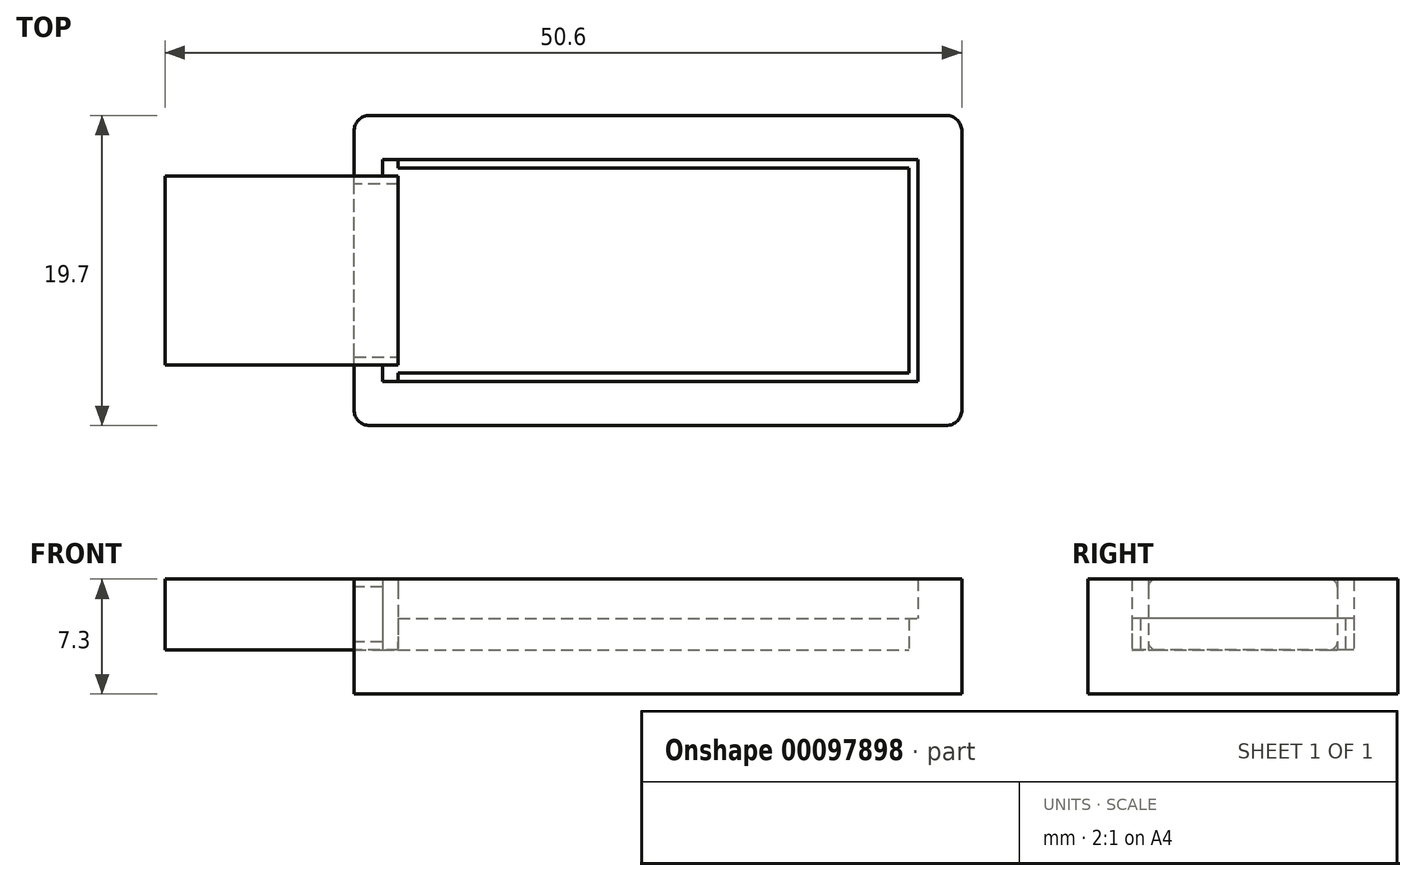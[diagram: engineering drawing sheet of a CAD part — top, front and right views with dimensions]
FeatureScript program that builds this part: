
annotation { "Feature Type Name" : "Feature", "Feature Type Description" : "" }
export const myFeature = defineFeature(function(context is Context, id is Id, definition is map)
    precondition{}
    {
        {
            var Q0;
            Q0=qCreatedBy(makeId("Top.planeOp"),FACE);
            var sketch = newSketch(context, id + "F0", { "sketchPlane" : qUnion([Q0])});
            skLineSegment(sketch, "E0.bottom", {"start": v(-43.45, 19.68) * mm, "end": v(-9.45, 19.68) * mm});
            skLineSegment(sketch, "E0.top", {"start": v(-43.45, 5.58) * mm, "end": v(-9.45, 5.58) * mm});
            skLineSegment(sketch, "E0.left", {"start": v(-42.45, 19.68) * mm, "end": v(-42.45, 18.63) * mm});
            skLineSegment(sketch, "E0.right", {"start": v(-9.45, 19.68) * mm, "end": v(-9.45, 5.58) * mm});
            skPoint(sketch, "E1", {"position": v(-42.45, 12.63) * mm});
            skLineSegment(sketch, "E2.bottom", {"start": v(-42.45, 12.63) * mm, "end": v(-57.25, 12.63) * mm});
            skLineSegment(sketch, "E2.top", {"start": v(-42.45, 18.63) * mm, "end": v(-57.25, 18.63) * mm});
            skLineSegment(sketch, "E2.left", {"start": v(-42.45, 12.63) * mm, "end": v(-42.45, 18.63) * mm});
            skLineSegment(sketch, "E2.right", {"start": v(-57.25, 12.63) * mm, "end": v(-57.25, 18.63) * mm});
            skLineSegment(sketch, "E3", {"start": v(-57.25, 12.63) * mm, "end": v(-57.25, 6.63) * mm});
            skLineSegment(sketch, "E4", {"start": v(-57.25, 6.63) * mm, "end": v(-42.45, 6.63) * mm});
            skLineSegment(sketch, "E5", {"start": v(-42.45, 18.63) * mm, "end": v(-42.45, 18.63) * mm});
            skLineSegment(sketch, "E6", {"start": v(-42.45, 18.63) * mm, "end": v(-42.45, 6.63) * mm});
            skLineSegment(sketch, "E7", {"start": v(-42.45, 6.63) * mm, "end": v(-42.45, 5.58) * mm});
            skLineSegment(sketch, "E8.0", {"start": v(-45.25, 22.48) * mm, "end": v(-45.25, 18.63) * mm});
            skLineSegment(sketch, "E8.1", {"start": v(-45.25, 6.63) * mm, "end": v(-45.25, 2.78) * mm});
            skLineSegment(sketch, "E8.2", {"start": v(-45.25, 2.78) * mm, "end": v(-6.65, 2.78) * mm});
            skLineSegment(sketch, "E8.3", {"start": v(-6.65, 22.48) * mm, "end": v(-6.65, 2.78) * mm});
            skLineSegment(sketch, "E8.4", {"start": v(-45.25, 22.48) * mm, "end": v(-6.65, 22.48) * mm});
            skLineSegment(sketch, "E9.0", {"start": v(-42.45, 6.13) * mm, "end": v(-10, 6.13) * mm});
            skLineSegment(sketch, "E9.1", {"start": v(-10, 19.13) * mm, "end": v(-10, 6.13) * mm});
            skLineSegment(sketch, "E9.2", {"start": v(-42.45, 19.13) * mm, "end": v(-10, 19.13) * mm});
            skLineSegment(sketch, "E10", {"start": v(-43.45, 19.68) * mm, "end": v(-43.45, 18.63) * mm});
            skLineSegment(sketch, "E11", {"start": v(-43.45, 5.58) * mm, "end": v(-43.45, 6.63) * mm});
            skSolve(sketch);
        }
        {
            var Q0;
            {var subQ5=sQuery(id+"F0.wireOp",EDGE,"E2.bottom");Q0=makeQuery(id+"F0.imprint","IMPRINT",FACE,{"disambiguationData":[TD([[makeQuery(id+"F0.imprint","IMPRINT",EDGE,{"derivedFrom":subQ5}),-1.0]])]});}
            var Q1;
            {var subQ5=sQuery(id+"F0.wireOp",EDGE,"E2.bottom");Q1=makeQuery(id+"F0.imprint","IMPRINT",FACE,{"disambiguationData":[TD([[makeQuery(id+"F0.imprint","IMPRINT",EDGE,{"derivedFrom":subQ5}),1.0]])]});}
            extrude(context, id + "F1", {"entities" : qUnion([Q0, Q1]), "depth" : 4.5 * mm});
        }
        {
            var Q0;
            Q0=makeQuery(id+"F1.opExtrude","CAP_EDGE",EDGE,{"disambiguationData":[OSD([sQuery(id+"F0.wireOp",EDGE,"E4")])],"isStart":false});
            var Q1;
            Q1=makeQuery(id+"F1.opExtrude","CAP_EDGE",EDGE,{"disambiguationData":[OSD([sQuery(id+"F0.wireOp",EDGE,"E4")])],"isStart":true});
            var Q2;
            Q2=makeQuery(id+"F1.opExtrude","CAP_EDGE",EDGE,{"disambiguationData":[OSD([sQuery(id+"F0.wireOp",EDGE,"E2.top")])],"isStart":true});
            var Q3;
            Q3=makeQuery(id+"F1.opExtrude","CAP_EDGE",EDGE,{"disambiguationData":[OSD([sQuery(id+"F0.wireOp",EDGE,"E2.top")])],"isStart":false});
            fillet(context, id + "F2", {"entities" : qUnion([Q0, Q1, Q2, Q3]), "radius" : .5 * mm, "tangentPropagation" : true, "allowEdgeOverflow" : false});
        }
        {
            var Q0;
            Q0=qCreatedBy(makeId("Top.planeOp"),FACE);
            var sketch = newSketch(context, id + "F3", { "sketchPlane" : qUnion([Q0])});
            skPoint(sketch, "E12.0", {"position": v(-45.25, 2.78) * mm});
            skPoint(sketch, "E12.1", {"position": v(-6.65, 2.78) * mm});
            skPoint(sketch, "E12.2", {"position": v(-6.65, 22.48) * mm});
            skPoint(sketch, "E12.3", {"position": v(-45.25, 22.48) * mm});
            skLineSegment(sketch, "E13.bottom", {"start": v(-45.25, 2.78) * mm, "end": v(-6.65, 2.78) * mm});
            skLineSegment(sketch, "E13.top", {"start": v(-45.25, 22.48) * mm, "end": v(-6.65, 22.48) * mm});
            skLineSegment(sketch, "E13.left", {"start": v(-45.25, 2.78) * mm, "end": v(-45.25, 22.48) * mm});
            skLineSegment(sketch, "E13.right", {"start": v(-6.65, 2.78) * mm, "end": v(-6.65, 22.48) * mm});
            skSolve(sketch);
        }
        {
            var Q0;
            Q0 = qSketchRegion(id + "F3", true);
            extrude(context, id + "F4", {"entities" : qUnion([Q0]), "oppositeDirection" : true, "depth" : 2.8 * mm});
        }
        {
            var Q0;
            {var subQ11=sQuery(id+"F0.wireOp",EDGE,"E0.bottom");Q0=makeQuery(id+"F0.imprint","IMPRINT",FACE,{"disambiguationData":[TD([[makeQuery(id+"F0.imprint","IMPRINT",EDGE,{"derivedFrom":subQ11}),1.0]])]});}
            extrude(context, id + "F5", {"entities" : qUnion([Q0]), "operationType" : NewBodyOperationType.ADD, "depth" : 4.5 * mm});
        }
        {
            var Q0;
            {var subQ0=sQuery(id+"F0.wireOp",EDGE,"E0.right");Q0=makeQuery(id+"F0.imprint","IMPRINT",FACE,{"disambiguationData":[TD([[makeQuery(id+"F0.imprint","IMPRINT",EDGE,{"derivedFrom":subQ0}),-1.0]])]});}
            extrude(context, id + "F6", {"entities" : qUnion([Q0]), "operationType" : NewBodyOperationType.ADD, "depth" : 2 * mm});
        }
        {
            var Q0;
            Q0=makeQuery(id+"F5.opExtrude","SWEPT_FACE",FACE,{"disambiguationData":[OSD([sQuery(id+"F0.wireOp",EDGE,"E0.right")])]});
            var sketch = newSketch(context, id + "F7", { "sketchPlane" : qUnion([Q0])});
            skLineSegment(sketch, "E14.0", {"start": v(-19.68, 4.5) * mm, "end": v(-5.58, 4.5) * mm});
            skLineSegment(sketch, "E14.1", {"start": v(-19.68, 4.5) * mm, "end": v(-19.68, 2.8) * mm});
            skLineSegment(sketch, "E14.2", {"start": v(-5.58, 4.5) * mm, "end": v(-5.58, 2.8) * mm});
            skPoint(sketch, "E15.end.orphan", {"position": v(-19.68, 2) * mm});
            skPoint(sketch, "E16.end.orphan", {"position": v(-5.58, 2) * mm});
            skLineSegment(sketch, "E17", {"start": v(-19.68, 2.8) * mm, "end": v(-5.58, 2.8) * mm});
            skSolve(sketch);
        }
        {
            var Q0;
            Q0=makeQuery(id+"F5.boolean.opBoolean","MERGE",EDGE,{"derivedFrom":[makeQuery(id+"F4.opExtrude","SWEPT_EDGE",EDGE,{"disambiguationData":[OSD([sQuery(id+"F3.wireOp",EDGE,"E13.bottom"),sQuery(id+"F3.wireOp",EDGE,"E13.left")])]}),makeQuery(id+"F5.opExtrude","SWEPT_EDGE",EDGE,{"disambiguationData":[OSD([sQuery(id+"F0.wireOp",EDGE,"E8.1"),sQuery(id+"F0.wireOp",EDGE,"E8.2")])]})]});
            var Q1;
            Q1=makeQuery(id+"F5.boolean.opBoolean","MERGE",EDGE,{"derivedFrom":[makeQuery(id+"F4.opExtrude","SWEPT_EDGE",EDGE,{"disambiguationData":[OSD([sQuery(id+"F3.wireOp",EDGE,"E13.top"),sQuery(id+"F3.wireOp",EDGE,"E13.left")])]}),makeQuery(id+"F5.opExtrude","SWEPT_EDGE",EDGE,{"disambiguationData":[OSD([sQuery(id+"F0.wireOp",EDGE,"E8.0"),sQuery(id+"F0.wireOp",EDGE,"E8.4")])]})]});
            var Q2;
            Q2=makeQuery(id+"F5.boolean.opBoolean","MERGE",EDGE,{"derivedFrom":[makeQuery(id+"F4.opExtrude","SWEPT_EDGE",EDGE,{"disambiguationData":[OSD([sQuery(id+"F3.wireOp",EDGE,"E13.top"),sQuery(id+"F3.wireOp",EDGE,"E13.right")])]}),makeQuery(id+"F5.opExtrude","SWEPT_EDGE",EDGE,{"disambiguationData":[OSD([sQuery(id+"F0.wireOp",EDGE,"E8.3"),sQuery(id+"F0.wireOp",EDGE,"E8.4")])]})]});
            var Q3;
            Q3=makeQuery(id+"F5.boolean.opBoolean","MERGE",EDGE,{"derivedFrom":[makeQuery(id+"F4.opExtrude","SWEPT_EDGE",EDGE,{"disambiguationData":[OSD([sQuery(id+"F3.wireOp",EDGE,"E13.bottom"),sQuery(id+"F3.wireOp",EDGE,"E13.right")])]}),makeQuery(id+"F5.opExtrude","SWEPT_EDGE",EDGE,{"disambiguationData":[OSD([sQuery(id+"F0.wireOp",EDGE,"E8.2"),sQuery(id+"F0.wireOp",EDGE,"E8.3")])]})]});
            fillet(context, id + "F8", {"entities" : qUnion([Q0, Q1, Q2, Q3]), "radius" : 1 * mm, "tangentPropagation" : true, "allowEdgeOverflow" : false});
        }
    });
